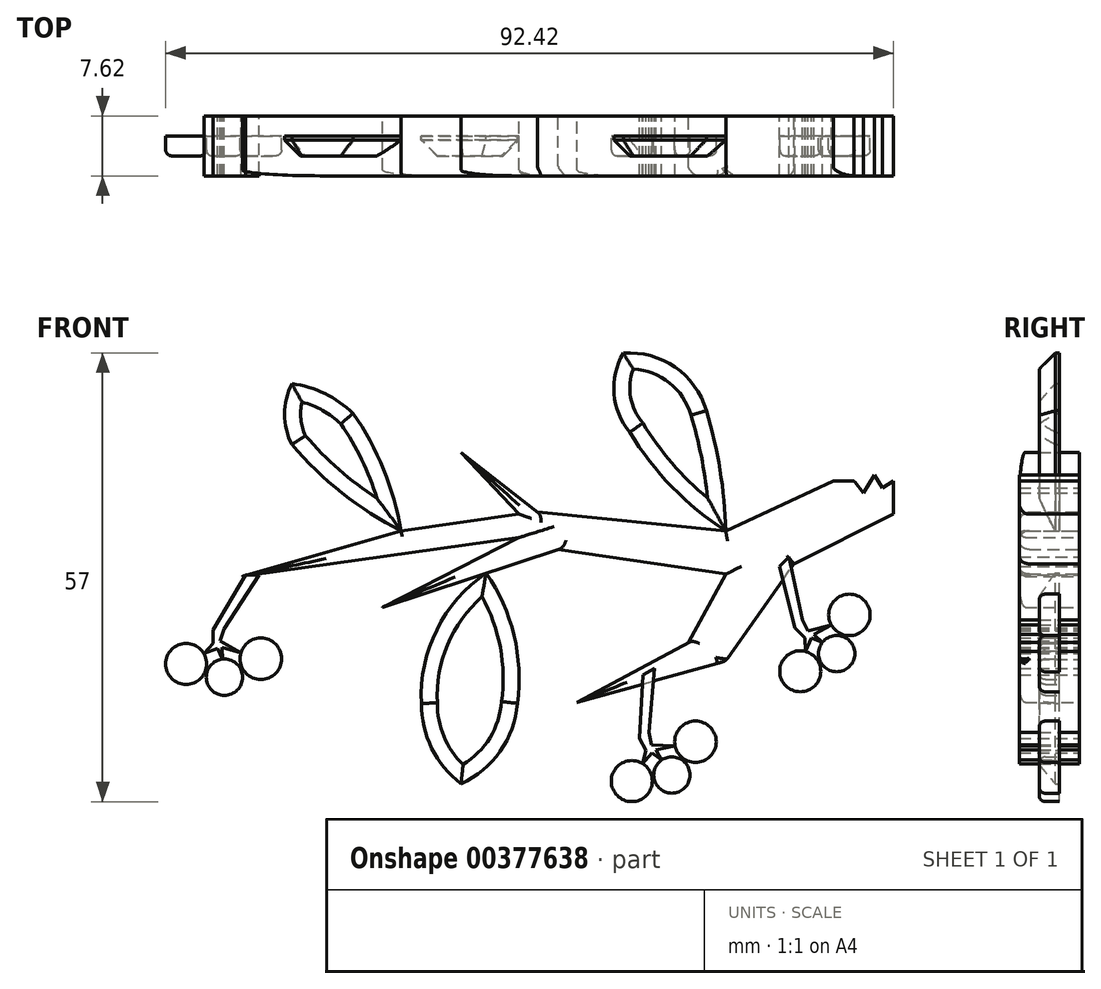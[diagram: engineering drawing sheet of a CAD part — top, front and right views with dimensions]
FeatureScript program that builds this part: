
annotation { "Feature Type Name" : "Feature", "Feature Type Description" : "" }
export const myFeature = defineFeature(function(context is Context, id is Id, definition is map)
    precondition{}
    {
        {
            var Q0;
            Q0=qCreatedBy(makeId("Front.planeOp"),FACE);
            var sketch = newSketch(context, id + "F0", { "sketchPlane" : qUnion([Q0])});
            skLineSegment(sketch, "E0", {"start": v(47.3, 65.56) * mm, "end": v(33.63, 59.25) * mm});
            skLineSegment(sketch, "E1", {"start": v(33.63, 59.25) * mm, "end": v(9.72, 61.62) * mm});
            skLineSegment(sketch, "E2", {"start": v(9.72, 61.62) * mm, "end": v(0, 69.23) * mm});
            skLineSegment(sketch, "E3", {"start": v(0, 69.23) * mm, "end": v(7.4, 61.35) * mm});
            skLineSegment(sketch, "E4", {"start": v(7.4, 61.35) * mm, "end": v(-7.6, 59.25) * mm});
            skLineSegment(sketch, "E5", {"start": v(-7.6, 59.25) * mm, "end": v(-27.77, 53.46) * mm});
            skLineSegment(sketch, "E6", {"start": v(-27.77, 53.46) * mm, "end": v(-16.5, 55.04) * mm});
            skLineSegment(sketch, "E7", {"start": v(-16.5, 55.04) * mm, "end": v(7.4, 58.39) * mm});
            skLineSegment(sketch, "E8", {"start": v(7.4, 58.39) * mm, "end": v(-9.98, 49.53) * mm});
            skLineSegment(sketch, "E9", {"start": v(-9.98, 49.53) * mm, "end": v(12.35, 56.89) * mm});
            skLineSegment(sketch, "E10", {"start": v(12.35, 56.89) * mm, "end": v(33.63, 53.73) * mm});
            skLineSegment(sketch, "E11", {"start": v(33.63, 53.73) * mm, "end": v(28.9, 45.06) * mm});
            skLineSegment(sketch, "E12", {"start": v(28.9, 45.06) * mm, "end": v(14.71, 37.44) * mm});
            skLineSegment(sketch, "E13", {"start": v(14.71, 37.44) * mm, "end": v(33.63, 42.7) * mm});
            skLineSegment(sketch, "E14", {"start": v(33.63, 42.7) * mm, "end": v(42.3, 55.05) * mm});
            skLineSegment(sketch, "E15", {"start": v(42.3, 55.05) * mm, "end": v(54.92, 61.35) * mm});
            skLineSegment(sketch, "E16", {"start": v(54.92, 61.35) * mm, "end": v(54.92, 65.56) * mm});
            skLineSegment(sketch, "E17", {"start": v(54.92, 65.56) * mm, "end": v(53.55, 64.7) * mm});
            skLineSegment(sketch, "E18", {"start": v(53.55, 64.7) * mm, "end": v(52.53, 66.32) * mm});
            skLineSegment(sketch, "E19", {"start": v(52.53, 66.32) * mm, "end": v(51.14, 64.05) * mm});
            skLineSegment(sketch, "E20", {"start": v(51.14, 64.05) * mm, "end": v(49.93, 65.56) * mm});
            skLineSegment(sketch, "E21", {"start": v(49.93, 65.56) * mm, "end": v(47.3, 65.56) * mm});
            skArc(sketch, "E22", {"start": v(-21.47, 70.2) * mm, "mid": v(-15.08, 64.04) * mm, "end": v(-7.6, 59.25) * mm});
            skArc(sketch, "E23", {"start": v(-21.47, 77.93) * mm, "mid": v(-22.4, 74.07) * mm, "end": v(-21.47, 70.2) * mm});
            skArc(sketch, "E24", {"start": v(-13.7, 74.17) * mm, "mid": v(-17.28, 76.68) * mm, "end": v(-21.47, 77.93) * mm});
            skArc(sketch, "E25", {"start": v(-7.6, 59.25) * mm, "mid": v(-9.83, 67.05) * mm, "end": v(-13.7, 74.17) * mm});
            skArc(sketch, "E26", {"start": v(21.45, 71.75) * mm, "mid": v(26.83, 64.8) * mm, "end": v(33.63, 59.25) * mm});
            skArc(sketch, "E27", {"start": v(20.62, 81.8) * mm, "mid": v(19.45, 76.65) * mm, "end": v(21.45, 71.75) * mm});
            skArc(sketch, "E28", {"start": v(31.16, 74.5) * mm, "mid": v(27.2, 80.04) * mm, "end": v(20.62, 81.8) * mm});
            skArc(sketch, "E29", {"start": v(33.63, 59.25) * mm, "mid": v(32.91, 66.96) * mm, "end": v(31.16, 74.5) * mm});
            skArc(sketch, "E30", {"start": v(7.18, 37.33) * mm, "mid": v(6.74, 45.97) * mm, "end": v(3.2, 53.87) * mm});
            skArc(sketch, "E31", {"start": v(0, 27.11) * mm, "mid": v(4.98, 31.24) * mm, "end": v(7.18, 37.33) * mm});
            skArc(sketch, "E32", {"start": v(-5.04, 37.33) * mm, "mid": v(-3.7, 31.63) * mm, "end": v(0, 27.11) * mm});
            skArc(sketch, "E33", {"start": v(3.2, 53.87) * mm, "mid": v(-3.07, 46.67) * mm, "end": v(-5.04, 37.33) * mm});
            skSolve(sketch);
        }
        {
            var Q0;
            Q0=qCreatedBy(makeId("Front.planeOp"),FACE);
            var sketch = newSketch(context, id + "F1", { "sketchPlane" : qUnion([Q0])});
            skLineSegment(sketch, "E34", {"start": v(-27.35, 53.63) * mm, "end": v(-31.48, 46.67) * mm});
            skLineSegment(sketch, "E35", {"start": v(-31.48, 46.67) * mm, "end": v(-31.48, 44.92) * mm});
            skLineSegment(sketch, "E36", {"start": v(-31.48, 44.92) * mm, "end": v(-32.66, 43.66) * mm});
            skLineSegment(sketch, "E37", {"start": v(-32.66, 43.66) * mm, "end": v(-31.48, 44.92) * mm});
            skLineSegment(sketch, "E38", {"start": v(-32.66, 43.66) * mm, "end": v(-30.94, 44.33) * mm});
            skLineSegment(sketch, "E39", {"start": v(-30.94, 44.33) * mm, "end": v(-30.3, 42.94) * mm});
            skLineSegment(sketch, "E40", {"start": v(-30.3, 42.94) * mm, "end": v(-30.35, 44.42) * mm});
            skLineSegment(sketch, "E41", {"start": v(-30.35, 44.42) * mm, "end": v(-27.95, 43.72) * mm});
            skLineSegment(sketch, "E42", {"start": v(-27.95, 43.72) * mm, "end": v(-30.57, 45.26) * mm});
            skLineSegment(sketch, "E43", {"start": v(-30.57, 45.26) * mm, "end": v(-30.07, 46.78) * mm});
            skLineSegment(sketch, "E44", {"start": v(-30.07, 46.78) * mm, "end": v(-25.67, 53.63) * mm});
            skLineSegment(sketch, "E45", {"start": v(-25.67, 53.63) * mm, "end": v(-27.35, 53.63) * mm});
            skCircle(sketch, "E46", {"center": v(-30.04, 40.65) * mm, "radius": 2.3 * mm});
            skPoint(sketch, "E46.second.point", {"position": v(-30.99, 38.55) * mm});
            skPoint(sketch, "E46.third.point", {"position": v(-28.61, 38.84) * mm});
            skCircle(sketch, "E47", {"center": v(-25.42, 42.98) * mm, "radius": 2.64 * mm});
            skPoint(sketch, "E47.second.point", {"position": v(-22.88, 42.25) * mm});
            skPoint(sketch, "E47.third.point", {"position": v(-22.88, 42.25) * mm});
            skCircle(sketch, "E48", {"center": v(-34.9, 42.34) * mm, "radius": 2.6 * mm});
            skPoint(sketch, "E48.second.point", {"position": v(-37.48, 42.73) * mm});
            skPoint(sketch, "E48.third.point", {"position": v(-34.62, 39.75) * mm});
            skLineSegment(sketch, "E49", {"start": v(23.12, 40.95) * mm, "end": v(22.7, 32.87) * mm});
            skLineSegment(sketch, "E50", {"start": v(22.7, 32.87) * mm, "end": v(23.52, 31.33) * mm});
            skLineSegment(sketch, "E51", {"start": v(23.52, 31.33) * mm, "end": v(23.07, 29.66) * mm});
            skLineSegment(sketch, "E52", {"start": v(23.07, 29.66) * mm, "end": v(23.52, 31.33) * mm});
            skLineSegment(sketch, "E53", {"start": v(23.07, 29.66) * mm, "end": v(24.28, 31.05) * mm});
            skLineSegment(sketch, "E54", {"start": v(24.28, 31.05) * mm, "end": v(25.5, 30.12) * mm});
            skLineSegment(sketch, "E55", {"start": v(25.5, 30.12) * mm, "end": v(24.76, 31.41) * mm});
            skLineSegment(sketch, "E56", {"start": v(24.76, 31.41) * mm, "end": v(27.2, 31.9) * mm});
            skLineSegment(sketch, "E57", {"start": v(27.2, 31.9) * mm, "end": v(24.17, 32.04) * mm});
            skLineSegment(sketch, "E58", {"start": v(24.17, 32.04) * mm, "end": v(23.9, 33.62) * mm});
            skLineSegment(sketch, "E59", {"start": v(23.9, 33.62) * mm, "end": v(24.6, 41.74) * mm});
            skLineSegment(sketch, "E60", {"start": v(24.6, 41.74) * mm, "end": v(23.12, 40.95) * mm});
            skCircle(sketch, "E61", {"center": v(26.79, 28.21) * mm, "radius": 2.3 * mm});
            skPoint(sketch, "E61.second.point", {"position": v(26.93, 25.92) * mm});
            skPoint(sketch, "E61.third.point", {"position": v(28.9, 27.29) * mm});
            skCircle(sketch, "E62", {"center": v(29.8, 32.44) * mm, "radius": 2.64 * mm});
            skPoint(sketch, "E62.second.point", {"position": v(32.37, 32.97) * mm});
            skPoint(sketch, "E62.third.point", {"position": v(32.37, 32.97) * mm});
            skCircle(sketch, "E63", {"center": v(21.7, 27.45) * mm, "radius": 2.6 * mm});
            skPoint(sketch, "E63.second.point", {"position": v(19.24, 26.59) * mm});
            skPoint(sketch, "E63.third.point", {"position": v(23.16, 25.29) * mm});
            skLineSegment(sketch, "E64.0", {"start": v(23.12, 40.95) * mm, "end": v(24.6, 41.74) * mm, "construction": true});
            skLineSegment(sketch, "E65", {"start": v(40.45, 54.73) * mm, "end": v(42.46, 46.88) * mm});
            skLineSegment(sketch, "E66", {"start": v(42.46, 46.88) * mm, "end": v(43.69, 45.65) * mm});
            skLineSegment(sketch, "E67", {"start": v(43.69, 45.65) * mm, "end": v(43.75, 43.92) * mm});
            skLineSegment(sketch, "E68", {"start": v(43.75, 43.92) * mm, "end": v(43.69, 45.65) * mm});
            skLineSegment(sketch, "E69", {"start": v(43.75, 43.92) * mm, "end": v(44.5, 45.6) * mm});
            skLineSegment(sketch, "E70", {"start": v(44.5, 45.6) * mm, "end": v(45.93, 45.08) * mm});
            skLineSegment(sketch, "E71", {"start": v(45.93, 45.08) * mm, "end": v(44.84, 46.1) * mm});
            skLineSegment(sketch, "E72", {"start": v(44.84, 46.1) * mm, "end": v(47.04, 47.3) * mm});
            skLineSegment(sketch, "E73", {"start": v(47.04, 47.3) * mm, "end": v(44.1, 46.52) * mm});
            skLineSegment(sketch, "E74", {"start": v(44.1, 46.52) * mm, "end": v(43.37, 47.95) * mm});
            skLineSegment(sketch, "E75", {"start": v(43.37, 47.95) * mm, "end": v(41.64, 55.91) * mm});
            skLineSegment(sketch, "E76", {"start": v(41.64, 55.91) * mm, "end": v(40.45, 54.73) * mm});
            skCircle(sketch, "E77", {"center": v(47.73, 43.64) * mm, "radius": 2.3 * mm});
            skPoint(sketch, "E77.second.point", {"position": v(48.55, 41.49) * mm});
            skPoint(sketch, "E77.third.point", {"position": v(50.01, 43.38) * mm});
            skCircle(sketch, "E78", {"center": v(49.35, 48.57) * mm, "radius": 2.64 * mm});
            skPoint(sketch, "E78.second.point", {"position": v(51.66, 49.84) * mm});
            skPoint(sketch, "E78.third.point", {"position": v(51.66, 49.84) * mm});
            skCircle(sketch, "E79", {"center": v(43.1, 41.4) * mm, "radius": 2.6 * mm});
            skPoint(sketch, "E79.second.point", {"position": v(41, 39.86) * mm});
            skPoint(sketch, "E79.third.point", {"position": v(45.13, 39.77) * mm});
            skLineSegment(sketch, "E80.0", {"start": v(40.45, 54.73) * mm, "end": v(41.64, 55.91) * mm, "construction": true});
            skLineSegment(sketch, "E81", {"start": v(2.02, 66.84) * mm, "end": v(-3.77, 61.19) * mm});
            skLineSegment(sketch, "E82", {"start": v(-3.77, 61.19) * mm, "end": v(-4.23, 59.5) * mm});
            skLineSegment(sketch, "E83", {"start": v(-4.23, 59.5) * mm, "end": v(-5.69, 58.59) * mm});
            skLineSegment(sketch, "E84", {"start": v(-5.69, 58.59) * mm, "end": v(-4.23, 59.5) * mm});
            skLineSegment(sketch, "E85", {"start": v(-5.69, 58.59) * mm, "end": v(-3.86, 58.79) * mm});
            skLineSegment(sketch, "E86", {"start": v(-3.86, 58.79) * mm, "end": v(-3.6, 57.28) * mm});
            skLineSegment(sketch, "E87", {"start": v(-3.6, 57.28) * mm, "end": v(-3.26, 58.73) * mm});
            skLineSegment(sketch, "E88", {"start": v(-3.26, 58.73) * mm, "end": v(-1.13, 57.42) * mm});
            skLineSegment(sketch, "E89", {"start": v(-1.13, 57.42) * mm, "end": v(-3.26, 59.59) * mm});
            skLineSegment(sketch, "E90", {"start": v(-3.26, 59.59) * mm, "end": v(-2.39, 60.93) * mm});
            skLineSegment(sketch, "E91", {"start": v(-2.39, 60.93) * mm, "end": v(3.64, 66.4) * mm});
            skLineSegment(sketch, "E92", {"start": v(3.64, 66.4) * mm, "end": v(2.02, 66.84) * mm});
            skCircle(sketch, "E93", {"center": v(-3.94, 55) * mm, "radius": 2.3 * mm});
            skPoint(sketch, "E93.second.point", {"position": v(-5.4, 53.22) * mm});
            skPoint(sketch, "E93.third.point", {"position": v(-3.03, 52.89) * mm});
            skCircle(sketch, "E94", {"center": v(1.13, 56.06) * mm, "radius": 2.64 * mm});
            skPoint(sketch, "E94.second.point", {"position": v(3.4, 54.7) * mm});
            skPoint(sketch, "E94.third.point", {"position": v(3.4, 54.7) * mm});
            skCircle(sketch, "E95", {"center": v(-8.2, 57.9) * mm, "radius": 2.6 * mm});
            skPoint(sketch, "E95.second.point", {"position": v(-10.58, 58.93) * mm});
            skPoint(sketch, "E95.third.point", {"position": v(-8.6, 55.32) * mm});
            skLineSegment(sketch, "E96.0", {"start": v(2.02, 66.84) * mm, "end": v(3.64, 66.4) * mm, "construction": true});
            skSolve(sketch);
        }
        {
            var Q0;
            Q0=makeQuery(id+"F0.imprint","IMPRINT",FACE,{"disambiguationData":[TD([[makeQuery(id+"F0.imprint","IMPRINT",EDGE,{"derivedFrom":sQuery(id+"F0.wireOp",EDGE,"E0")}),1.0]])]});
            var Q1;
            Q1=makeQuery(id+"F1.imprint","IMPRINT",FACE,{"disambiguationData":[TD([[makeQuery(id+"F1.imprint","IMPRINT",EDGE,{"derivedFrom":sQuery(id+"F1.wireOp",EDGE,"E34")}),1.0]])]});
            var Q2;
            Q2=makeQuery(id+"F1.imprint","IMPRINT",FACE,{"disambiguationData":[TD([[makeQuery(id+"F1.imprint","IMPRINT",EDGE,{"derivedFrom":sQuery(id+"F1.wireOp",EDGE,"E49")}),1.0]])]});
            var Q3;
            Q3=makeQuery(id+"F1.imprint","IMPRINT",FACE,{"disambiguationData":[TD([[makeQuery(id+"F1.imprint","IMPRINT",EDGE,{"derivedFrom":sQuery(id+"F1.wireOp",EDGE,"E65")}),1.0]])]});
            var Q4;
            Q4=makeQuery(id+"F1.imprint","IMPRINT",FACE,{"disambiguationData":[TD([[makeQuery(id+"F1.imprint","IMPRINT",EDGE,{"derivedFrom":sQuery(id+"F1.wireOp",EDGE,"E81")}),1.0]])]});
            extrude(context, id + "F2", {"entities" : qUnion([Q0, Q1, Q2, Q3, Q4]), "endBound" : BoundingType.SYMMETRIC, "depth" : 7.62 * mm});
        }
        {
            var Q0;
            Q0=makeQuery(id+"F0.imprint","IMPRINT",FACE,{"disambiguationData":[TD([[makeQuery(id+"F0.imprint","IMPRINT",EDGE,{"derivedFrom":sQuery(id+"F0.wireOp",EDGE,"E22")}),1.0]])]});
            var Q1;
            Q1=makeQuery(id+"F0.imprint","IMPRINT",FACE,{"disambiguationData":[TD([[makeQuery(id+"F0.imprint","IMPRINT",EDGE,{"derivedFrom":sQuery(id+"F0.wireOp",EDGE,"E26")}),1.0]])]});
            var Q2;
            Q2=makeQuery(id+"F0.imprint","IMPRINT",FACE,{"disambiguationData":[TD([[makeQuery(id+"F0.imprint","IMPRINT",EDGE,{"derivedFrom":sQuery(id+"F0.wireOp",EDGE,"E30")}),1.0]])]});
            var Q3;
            Q3=makeQuery(id+"F1.imprint","IMPRINT",FACE,{"disambiguationData":[TD([[makeQuery(id+"F1.imprint","IMPRINT",EDGE,{"derivedFrom":sQuery(id+"F1.wireOp",EDGE,"E48")}),1.0]])]});
            var Q4;
            Q4=makeQuery(id+"F1.imprint","IMPRINT",FACE,{"disambiguationData":[TD([[makeQuery(id+"F1.imprint","IMPRINT",EDGE,{"derivedFrom":sQuery(id+"F1.wireOp",EDGE,"E46")}),1.0]])]});
            var Q5;
            Q5=makeQuery(id+"F1.imprint","IMPRINT",FACE,{"disambiguationData":[TD([[makeQuery(id+"F1.imprint","IMPRINT",EDGE,{"derivedFrom":sQuery(id+"F1.wireOp",EDGE,"E47")}),1.0]])]});
            var Q6;
            Q6=makeQuery(id+"F1.imprint","IMPRINT",FACE,{"disambiguationData":[TD([[makeQuery(id+"F1.imprint","IMPRINT",EDGE,{"derivedFrom":sQuery(id+"F1.wireOp",EDGE,"E93")}),1.0]])]});
            var Q7;
            Q7=makeQuery(id+"F1.imprint","IMPRINT",FACE,{"disambiguationData":[TD([[makeQuery(id+"F1.imprint","IMPRINT",EDGE,{"derivedFrom":sQuery(id+"F1.wireOp",EDGE,"E94")}),1.0]])]});
            var Q8;
            Q8=makeQuery(id+"F1.imprint","IMPRINT",FACE,{"disambiguationData":[TD([[makeQuery(id+"F1.imprint","IMPRINT",EDGE,{"derivedFrom":sQuery(id+"F1.wireOp",EDGE,"E63")}),1.0]])]});
            var Q9;
            Q9=makeQuery(id+"F1.imprint","IMPRINT",FACE,{"disambiguationData":[TD([[makeQuery(id+"F1.imprint","IMPRINT",EDGE,{"derivedFrom":sQuery(id+"F1.wireOp",EDGE,"E61")}),1.0]])]});
            var Q10;
            Q10=makeQuery(id+"F1.imprint","IMPRINT",FACE,{"disambiguationData":[TD([[makeQuery(id+"F1.imprint","IMPRINT",EDGE,{"derivedFrom":sQuery(id+"F1.wireOp",EDGE,"E62")}),1.0]])]});
            var Q11;
            Q11=makeQuery(id+"F1.imprint","IMPRINT",FACE,{"disambiguationData":[TD([[makeQuery(id+"F1.imprint","IMPRINT",EDGE,{"derivedFrom":sQuery(id+"F1.wireOp",EDGE,"E79")}),1.0]])]});
            var Q12;
            Q12=makeQuery(id+"F1.imprint","IMPRINT",FACE,{"disambiguationData":[TD([[makeQuery(id+"F1.imprint","IMPRINT",EDGE,{"derivedFrom":sQuery(id+"F1.wireOp",EDGE,"E77")}),1.0]])]});
            var Q13;
            Q13=makeQuery(id+"F1.imprint","IMPRINT",FACE,{"disambiguationData":[TD([[makeQuery(id+"F1.imprint","IMPRINT",EDGE,{"derivedFrom":sQuery(id+"F1.wireOp",EDGE,"E78")}),1.0]])]});
            var Q14;
            Q14=makeQuery(id+"F1.imprint","IMPRINT",FACE,{"disambiguationData":[TD([[makeQuery(id+"F1.imprint","IMPRINT",EDGE,{"derivedFrom":sQuery(id+"F1.wireOp",EDGE,"E95")}),1.0]])]});
            extrude(context, id + "F3", {"entities" : qUnion([Q0, Q1, Q2, Q3, Q4, Q5, Q6, Q7, Q8, Q9, Q10, Q11, Q12, Q13, Q14]), "endBound" : BoundingType.SYMMETRIC, "depth" : 2.54 * mm});
        }
        {
            var Q0;
            Q0=makeQuery(id+"F2.opExtrude","CAP_EDGE",EDGE,{"disambiguationData":[OSD([sQuery(id+"F0.wireOp",EDGE,"E4")])],"isStart":false});
            var Q1;
            Q1=makeQuery(id+"F2.opExtrude","CAP_EDGE",EDGE,{"disambiguationData":[OSD([sQuery(id+"F0.wireOp",EDGE,"E5")])],"isStart":false});
            var Q2;
            Q2=makeQuery(id+"F2.opExtrude","CAP_EDGE",EDGE,{"disambiguationData":[OSD([sQuery(id+"F0.wireOp",EDGE,"E6"),sQuery(id+"F0.wireOp",EDGE,"E7")])],"isStart":false});
            var Q3;
            Q3=makeQuery(id+"F2.opExtrude","CAP_EDGE",EDGE,{"disambiguationData":[OSD([sQuery(id+"F0.wireOp",EDGE,"E8")])],"isStart":false});
            var Q4;
            Q4=makeQuery(id+"F2.opExtrude","CAP_EDGE",EDGE,{"disambiguationData":[OSD([sQuery(id+"F0.wireOp",EDGE,"E9")])],"isStart":false});
            var Q5;
            Q5=makeQuery(id+"F2.opExtrude","CAP_EDGE",EDGE,{"disambiguationData":[OSD([sQuery(id+"F0.wireOp",EDGE,"E3")])],"isStart":false});
            var Q6;
            Q6=makeQuery(id+"F2.opExtrude","CAP_EDGE",EDGE,{"disambiguationData":[OSD([sQuery(id+"F0.wireOp",EDGE,"E2")])],"isStart":false});
            var Q7;
            Q7=makeQuery(id+"F2.opExtrude","CAP_EDGE",EDGE,{"disambiguationData":[OSD([sQuery(id+"F0.wireOp",EDGE,"E12")])],"isStart":false});
            var Q8;
            Q8=makeQuery(id+"F2.opExtrude","CAP_EDGE",EDGE,{"disambiguationData":[OSD([sQuery(id+"F0.wireOp",EDGE,"E13")])],"isStart":false});
            var Q9;
            Q9=makeQuery(id+"F3.opExtrude","CAP_EDGE",EDGE,{"disambiguationData":[OSD([sQuery(id+"F1.wireOp",EDGE,"E48")])],"isStart":false});
            var Q10;
            Q10=makeQuery(id+"F3.opExtrude","CAP_EDGE",EDGE,{"disambiguationData":[OSD([sQuery(id+"F1.wireOp",EDGE,"E46")])],"isStart":false});
            var Q11;
            Q11=makeQuery(id+"F3.opExtrude","CAP_EDGE",EDGE,{"disambiguationData":[OSD([sQuery(id+"F1.wireOp",EDGE,"E47")])],"isStart":false});
            var Q12;
            Q12=makeQuery(id+"F3.opExtrude","CAP_FACE",FACE,{"disambiguationData":[OSD([sQuery(id+"F1.wireOp",EDGE,"E93")])],"isStart":false});
            var Q13;
            Q13=makeQuery(id+"F3.opExtrude","CAP_EDGE",EDGE,{"disambiguationData":[OSD([sQuery(id+"F1.wireOp",EDGE,"E95")])],"isStart":false});
            var Q14;
            Q14=makeQuery(id+"F3.opExtrude","CAP_FACE",FACE,{"disambiguationData":[OSD([sQuery(id+"F1.wireOp",EDGE,"E94")])],"isStart":false});
            var Q15;
            Q15=makeQuery(id+"F3.opExtrude","CAP_FACE",FACE,{"disambiguationData":[OSD([sQuery(id+"F1.wireOp",EDGE,"E63")])],"isStart":false});
            var Q16;
            Q16=makeQuery(id+"F3.opExtrude","CAP_FACE",FACE,{"disambiguationData":[OSD([sQuery(id+"F1.wireOp",EDGE,"E61")])],"isStart":false});
            var Q17;
            Q17=makeQuery(id+"F3.opExtrude","CAP_FACE",FACE,{"disambiguationData":[OSD([sQuery(id+"F1.wireOp",EDGE,"E62")])],"isStart":false});
            var Q18;
            Q18=makeQuery(id+"F3.opExtrude","CAP_EDGE",EDGE,{"disambiguationData":[OSD([sQuery(id+"F1.wireOp",EDGE,"E79")])],"isStart":false});
            var Q19;
            Q19=makeQuery(id+"F3.opExtrude","CAP_FACE",FACE,{"disambiguationData":[OSD([sQuery(id+"F1.wireOp",EDGE,"E77")])],"isStart":false});
            var Q20;
            Q20=makeQuery(id+"F3.opExtrude","CAP_FACE",FACE,{"disambiguationData":[OSD([sQuery(id+"F1.wireOp",EDGE,"E78")])],"isStart":false});
            fillet(context, id + "F4", {"entities" : qUnion([Q0, Q1, Q2, Q3, Q4, Q5, Q6, Q7, Q8, Q9, Q10, Q11, Q12, Q13, Q14, Q15, Q16, Q17, Q18, Q19, Q20]), "radius" : 0.76 * mm, "tangentPropagation" : true, "allowEdgeOverflow" : false});
        }
        {
            var Q0;
            Q0=makeQuery(id+"F2.opExtrude","CAP_EDGE",EDGE,{"disambiguationData":[OSD([sQuery(id+"F0.wireOp",EDGE,"E1")])],"isStart":false});
            var Q1;
            Q1=makeQuery(id+"F2.opExtrude","CAP_EDGE",EDGE,{"disambiguationData":[OSD([sQuery(id+"F0.wireOp",EDGE,"E10")])],"isStart":false});
            var Q2;
            Q2=makeQuery(id+"F2.opExtrude","CAP_EDGE",EDGE,{"disambiguationData":[OSD([sQuery(id+"F0.wireOp",EDGE,"E0")])],"isStart":false});
            var Q3;
            Q3=makeQuery(id+"F2.opExtrude","CAP_EDGE",EDGE,{"disambiguationData":[OSD([sQuery(id+"F0.wireOp",EDGE,"E15")])],"isStart":false});
            var Q4;
            Q4=makeQuery(id+"F2.opExtrude","CAP_EDGE",EDGE,{"disambiguationData":[OSD([sQuery(id+"F0.wireOp",EDGE,"E14")])],"isStart":false});
            var Q5;
            Q5=makeQuery(id+"F2.opExtrude","CAP_EDGE",EDGE,{"disambiguationData":[OSD([sQuery(id+"F0.wireOp",EDGE,"E11")])],"isStart":false});
            fillet(context, id + "F5", {"entities" : qUnion([Q0, Q1, Q2, Q3, Q4, Q5]), "radius" : 1.27 * mm, "tangentPropagation" : true, "allowEdgeOverflow" : false});
        }
        {
            var Q0;
            Q0=makeQuery(id+"F3.opExtrude","CAP_FACE",FACE,{"disambiguationData":[OSD([sQuery(id+"F0.wireOp",EDGE,"E22"),sQuery(id+"F0.wireOp",EDGE,"E23"),sQuery(id+"F0.wireOp",EDGE,"E24"),sQuery(id+"F0.wireOp",EDGE,"E25")])],"isStart":false});
            var Q1;
            Q1=makeQuery(id+"F3.opExtrude","CAP_FACE",FACE,{"disambiguationData":[OSD([sQuery(id+"F0.wireOp",EDGE,"E30"),sQuery(id+"F0.wireOp",EDGE,"E31"),sQuery(id+"F0.wireOp",EDGE,"E32"),sQuery(id+"F0.wireOp",EDGE,"E33")])],"isStart":false});
            var Q2;
            Q2=makeQuery(id+"F3.opExtrude","CAP_FACE",FACE,{"disambiguationData":[OSD([sQuery(id+"F0.wireOp",EDGE,"E26"),sQuery(id+"F0.wireOp",EDGE,"E27"),sQuery(id+"F0.wireOp",EDGE,"E28"),sQuery(id+"F0.wireOp",EDGE,"E29")])],"isStart":false});
            chamfer(context, id + "F6", {"entities" : qUnion([Q0, Q1, Q2]), "width" : 2.03 * mm, "tangentPropagation" : true});
        }
        {
            var Q0;
            Q0=makeQuery(id+"F3.opExtrude","SWEPT_BODY",BODY,{"disambiguationData":[OSD([sQuery(id+"F1.wireOp",EDGE,"E95")])]});
            var Q1;
            Q1=makeQuery(id+"F3.opExtrude","SWEPT_BODY",BODY,{"disambiguationData":[OSD([sQuery(id+"F1.wireOp",EDGE,"E94")])]});
            var Q2;
            Q2=makeQuery(id+"F3.opExtrude","SWEPT_BODY",BODY,{"disambiguationData":[OSD([sQuery(id+"F1.wireOp",EDGE,"E93")])]});
            var Q3;
            Q3=makeQuery(id+"F2.opExtrude","SWEPT_BODY",BODY,{"disambiguationData":[OSD([sQuery(id+"F1.wireOp",EDGE,"E81"),sQuery(id+"F1.wireOp",EDGE,"E82"),sQuery(id+"F1.wireOp",EDGE,"E84"),sQuery(id+"F1.wireOp",EDGE,"E85"),sQuery(id+"F1.wireOp",EDGE,"E86"),sQuery(id+"F1.wireOp",EDGE,"E87"),sQuery(id+"F1.wireOp",EDGE,"E88"),sQuery(id+"F1.wireOp",EDGE,"E89"),sQuery(id+"F1.wireOp",EDGE,"E90"),sQuery(id+"F1.wireOp",EDGE,"E91"),sQuery(id+"F1.wireOp",EDGE,"E92")])]});
            deleteBodies(context, id + "F7", {"entities" : qUnion([Q0, Q1, Q2, Q3])});
        }
    });
